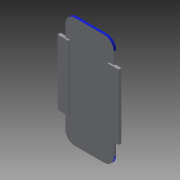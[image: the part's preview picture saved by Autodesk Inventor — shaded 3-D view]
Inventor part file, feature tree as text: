
AUTODESK INVENTOR PART (.ipt)
format: ipt  version: 2015 (Build 190159000, 159)  size: 123,904 bytes
history: native  units: mm
features: extrude x4, sketch x2, fillet x1
ambient origin geometry x8: Origin, YZ Plane, XZ Plane, XY Plane, X Axis, Y Axis, Z Axis, Center Point
bodies: Solid1 (feature_tree)
feature tree (7):
  extrude  "Extrusion1"  Depth=101.2mm
  fillet  "Fillet1"  Radius=5.0mm
  extrude  "Extrusion3"  Depth=45.0mm
  extrude  "Extrusion4"  Depth=10.0mm
  extrude  "Extrusion5"  Depth=136.0mm
  sketch  "Sketch3"  dims[d0=231.3mm d1=101.2mm d2=5.0mm d3=0.0mm]
  sketch  "Sketch4"  dims[d4=20.0mm d14=45.0mm d18=10.0mm d19=136.0mm d20=3.0mm d21=0.0mm d22=136.0mm d23=6.0mm d24=13.0mm d25=0.0mm d26=136.0mm d27=6.0mm d28=13.0mm d29=0.0mm]
